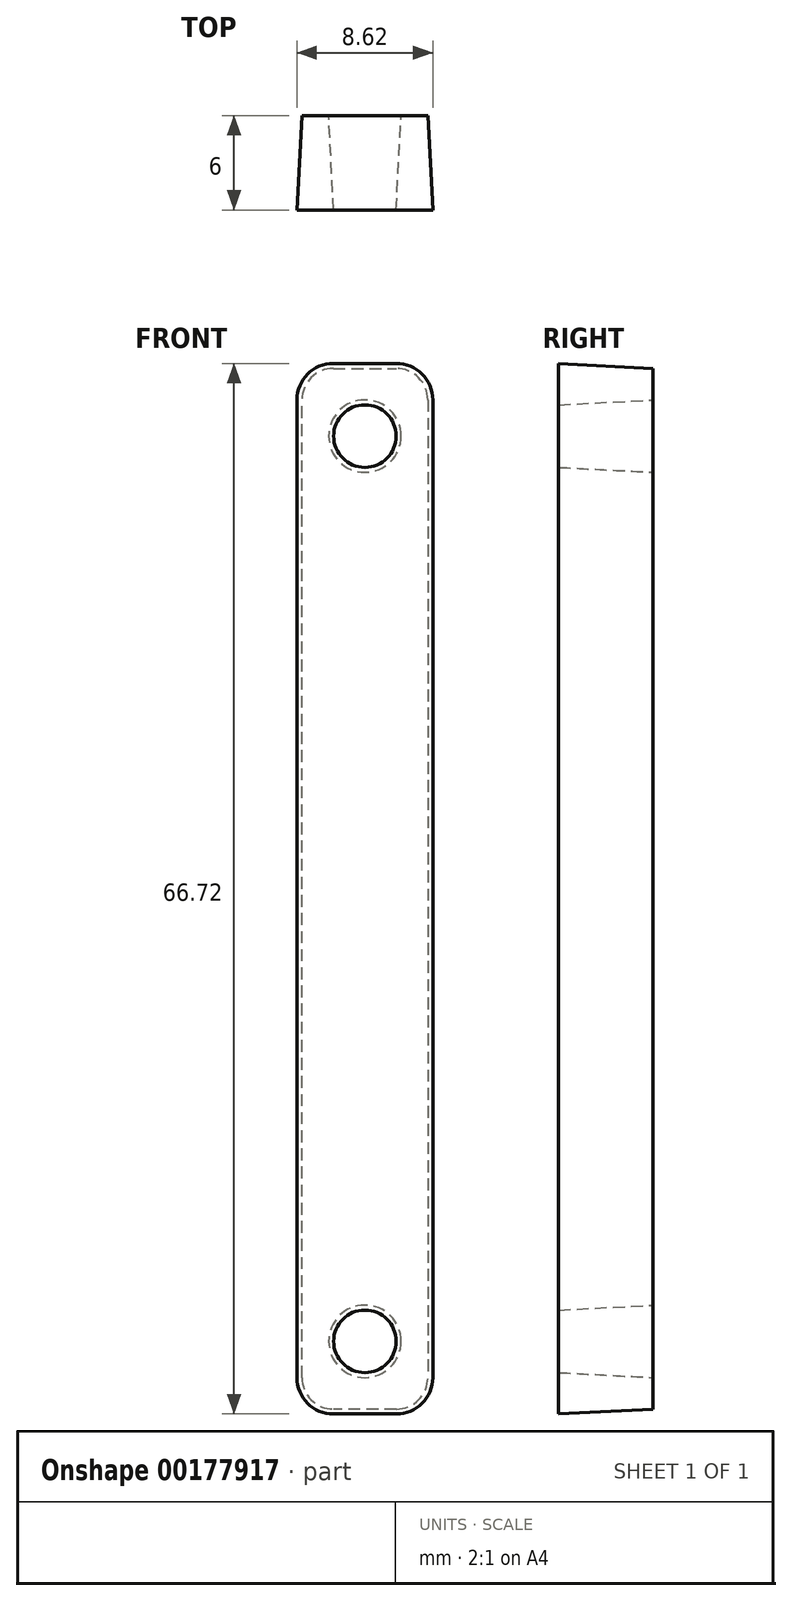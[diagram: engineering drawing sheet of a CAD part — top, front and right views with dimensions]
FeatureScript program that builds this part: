
annotation { "Feature Type Name" : "Feature", "Feature Type Description" : "" }
export const myFeature = defineFeature(function(context is Context, id is Id, definition is map)
    precondition{}
    {
        {
            var Q0;
            Q0=qCreatedBy(makeId("Front.planeOp"),FACE);
            var sketch = newSketch(context, id + "F0", { "sketchPlane" : qUnion([Q0])});
            skLineSegment(sketch, "E0.bottom", {"start": v(2, 0) * mm, "end": v(6, 0) * mm});
            skLineSegment(sketch, "E0.top", {"start": v(2, 66.1) * mm, "end": v(6, 66.1) * mm});
            skLineSegment(sketch, "E0.left", {"start": v(0, 2) * mm, "end": v(0, 64.1) * mm});
            skLineSegment(sketch, "E0.right", {"start": v(8, 2) * mm, "end": v(8, 64.1) * mm});
            skLineSegment(sketch, "E1", {"start": v(4, 66.1) * mm, "end": v(4, 0) * mm});
            skCircle(sketch, "E2", {"center": v(4, 4.3) * mm, "radius": 2.3 * mm});
            skCircle(sketch, "E3", {"center": v(4, 61.8) * mm, "radius": 2.3 * mm});
            skPoint(sketch, "E4", {"position": v(4, 64.1) * mm});
            skPoint(sketch, "E5", {"position": v(4, 59.5) * mm});
            skPoint(sketch, "E6", {"position": v(4, 2) * mm});
            skPoint(sketch, "E7", {"position": v(4, 6.6) * mm});
            skPoint(sketch, "E8.visualSharp", {"position": v(0, 0) * mm});
            skArc(sketch, "E8.filletArc", {"start": v(0, 2) * mm, "mid": v(0.59, 0.59) * mm, "end": v(2, 0) * mm});
            skPoint(sketch, "E9.visualSharp", {"position": v(8, 0) * mm});
            skArc(sketch, "E9.filletArc", {"start": v(6, 0) * mm, "mid": v(7.41, 0.59) * mm, "end": v(8, 2) * mm});
            skPoint(sketch, "E10.visualSharp", {"position": v(8, 66.1) * mm});
            skArc(sketch, "E10.filletArc", {"start": v(8, 64.1) * mm, "mid": v(7.41, 65.51) * mm, "end": v(6, 66.1) * mm});
            skPoint(sketch, "E11.visualSharp", {"position": v(0, 66.1) * mm});
            skArc(sketch, "E11.filletArc", {"start": v(2, 66.1) * mm, "mid": v(0.59, 65.51) * mm, "end": v(0, 64.1) * mm});
            skSolve(sketch);
        }
        {
            var Q0;
            Q0=makeQuery(id+"F0.imprint","IMPRINT",FACE,{"disambiguationData":[TD([[makeQuery(id+"F0.imprint","IMPRINT",EDGE,{"derivedFrom":sQuery(id+"F0.wireOp",EDGE,"E0.left")}),-1.0]])]});
            var Q1;
            Q1=makeQuery(id+"F0.imprint","IMPRINT",FACE,{"disambiguationData":[TD([[makeQuery(id+"F0.imprint","IMPRINT",EDGE,{"derivedFrom":sQuery(id+"F0.wireOp",EDGE,"E0.right")}),1.0]])]});
            extrude(context, id + "F1", {"entities" : qUnion([Q0, Q1]), "depth" : 6 * mm, "hasDraft" : true, "draftAngle" : 3 * degree});
        }
    });
